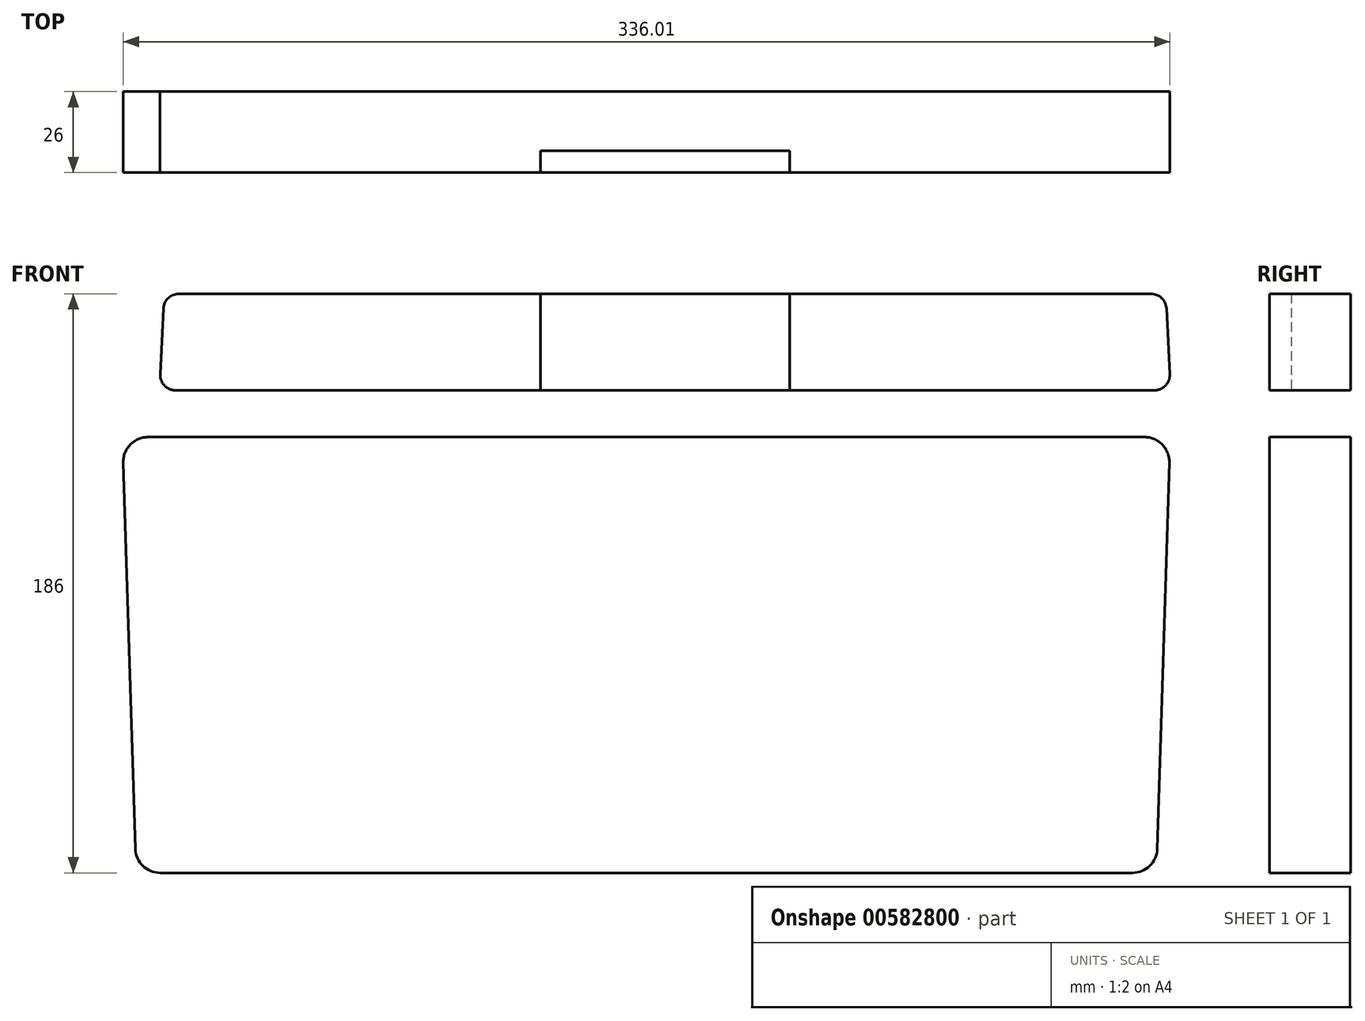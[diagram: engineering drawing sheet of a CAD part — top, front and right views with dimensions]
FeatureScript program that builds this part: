
annotation { "Feature Type Name" : "Feature", "Feature Type Description" : "" }
export const myFeature = defineFeature(function(context is Context, id is Id, definition is map)
    precondition{}
    {
        {
            var Q0;
            Q0=qCreatedBy(makeId("Front.planeOp"),FACE);
            var sketch = newSketch(context, id + "F0", { "sketchPlane" : qUnion([Q0])});
            skLineSegment(sketch, "E0.bottom", {"start": v(172.5, -161) * mm, "end": v(-172.5, -161) * mm});
            skLineSegment(sketch, "E0.top", {"start": v(177.5, -1) * mm, "end": v(-177.5, -1) * mm});
            skLineSegment(sketch, "E1.bottom", {"start": v(177.5, 1) * mm, "end": v(-177.5, 1) * mm});
            skLineSegment(sketch, "E1.top", {"start": v(175, 51) * mm, "end": v(-175, 51) * mm});
            skLineSegment(sketch, "E2", {"start": v(-177.5, -1) * mm, "end": v(-172.5, -161) * mm});
            skLineSegment(sketch, "E3", {"start": v(177.5, -1) * mm, "end": v(172.5, -161) * mm});
            skLineSegment(sketch, "E4", {"start": v(-177.5, 1) * mm, "end": v(-175, 51) * mm});
            skLineSegment(sketch, "E5", {"start": v(177.5, 1) * mm, "end": v(175, 51) * mm});
            skLineSegment(sketch, "E6.bottom", {"start": v(105.5, -101) * mm, "end": v(147.5, -101) * mm});
            skLineSegment(sketch, "E6.top", {"start": v(105.5, -161) * mm, "end": v(147.5, -161) * mm});
            skLineSegment(sketch, "E6.left", {"start": v(105.5, -101) * mm, "end": v(105.5, -161) * mm});
            skLineSegment(sketch, "E6.right", {"start": v(147.5, -101) * mm, "end": v(147.5, -161) * mm});
            skLineSegment(sketch, "E7.MirrorCS", {"start": v(-105.5, -101) * mm, "end": v(-105.5, -161) * mm});
            skLineSegment(sketch, "E8.MirrorCS", {"start": v(-105.5, -101) * mm, "end": v(-147.5, -101) * mm});
            skLineSegment(sketch, "E9.MirrorCS", {"start": v(-147.5, -101) * mm, "end": v(-147.5, -161) * mm});
            skSolve(sketch);
        }
        {
            var Q0;
            Q0=qCreatedBy(makeId("Front.planeOp"),FACE);
            var sketch = newSketch(context, id + "F1", { "sketchPlane" : qUnion([Q0])});
            skLineSegment(sketch, "E10", {"start": v(-159.68, -91) * mm, "end": v(-100.5, -91) * mm, "construction": true});
            skLineSegment(sketch, "E11", {"start": v(-100.5, -91) * mm, "end": v(-100.5, -151) * mm, "construction": true});
            skLineSegment(sketch, "E12", {"start": v(-100.5, -151) * mm, "end": v(100.5, -151) * mm});
            skLineSegment(sketch, "E13", {"start": v(100.5, -151) * mm, "end": v(100.5, -91) * mm, "construction": true});
            skLineSegment(sketch, "E14", {"start": v(100.5, -91) * mm, "end": v(152.5, -91) * mm, "construction": true});
            skLineSegment(sketch, "E15", {"start": v(152.5, -91) * mm, "end": v(152.5, -151) * mm, "construction": true});
            skLineSegment(sketch, "E16", {"start": v(152.5, -151) * mm, "end": v(169.81, -151) * mm});
            skLineSegment(sketch, "E17", {"start": v(169.81, -151) * mm, "end": v(174.19, -11) * mm});
            skLineSegment(sketch, "E18", {"start": v(174.19, -11) * mm, "end": v(-162.18, -11) * mm});
            skLineSegment(sketch, "E19", {"start": v(-162.18, -11) * mm, "end": v(-159.68, -91) * mm});
            skLineSegment(sketch, "E20", {"start": v(-159.68, -91) * mm, "end": v(-157.8, -151) * mm});
            skLineSegment(sketch, "E21", {"start": v(-157.8, -151) * mm, "end": v(-100.5, -151) * mm});
            skLineSegment(sketch, "E22", {"start": v(100.5, -151) * mm, "end": v(152.5, -151) * mm});
            skSolve(sketch);
        }
        {
            var Q0;
            Q0=qSketchRegion(id+"F1",true);
            extrude(context, id + "F2", {"entities" : qUnion([Q0]), "depth" : 26 * mm, "offsetDistance" : 25 * mm});
        }
        {
            var Q0;
            Q0=qCreatedBy(makeId("Front.planeOp"),FACE);
            var sketch = newSketch(context, id + "F3", { "sketchPlane" : qUnion([Q0])});
            skLineSegment(sketch, "E23.0", {"start": v(162.33, 4) * mm, "end": v(160.78, 35) * mm});
            skLineSegment(sketch, "E23.2", {"start": v(-162.33, 4) * mm, "end": v(-160.78, 35) * mm});
            skLineSegment(sketch, "E24", {"start": v(-160.78, 35) * mm, "end": v(160.78, 35) * mm});
            skLineSegment(sketch, "E25", {"start": v(-162.33, 4) * mm, "end": v(162.33, 4) * mm});
            skSolve(sketch);
        }
        {
            var Q0;
            Q0=qSketchRegion(id+"F3",true);
            var Q1;
            Q1=sQuery(id+"F3.wireOp",EDGE,"E24");
            var Q2;
            Q2=sQuery(id+"F3.wireOp",EDGE,"E23.2");
            var Q3;
            Q3=sQuery(id+"F3.wireOp",EDGE,"E25");
            var Q4;
            Q4=sQuery(id+"F3.wireOp",EDGE,"E23.0");
            extrude(context, id + "F4", {"entities" : qUnion([Q0]), "surfaceEntities" : qUnion([Q1, Q2, Q3, Q4]), "depth" : 26 * mm, "offsetDistance" : 25 * mm});
        }
        {
            var Q0;
            Q0=makeQuery(id+"F4.opExtrude","SWEPT_EDGE",EDGE,{"disambiguationData":[OSD([sQuery(id+"F3.wireOp",EDGE,"E23.2"),sQuery(id+"F3.wireOp",EDGE,"E24")])]});
            var Q1;
            Q1=makeQuery(id+"F4.opExtrude","SWEPT_EDGE",EDGE,{"disambiguationData":[OSD([sQuery(id+"F3.wireOp",EDGE,"E23.2"),sQuery(id+"F3.wireOp",EDGE,"E25")])]});
            var Q2;
            Q2=makeQuery(id+"F4.opExtrude","SWEPT_EDGE",EDGE,{"disambiguationData":[OSD([sQuery(id+"F3.wireOp",EDGE,"E23.0"),sQuery(id+"F3.wireOp",EDGE,"E24")])]});
            var Q3;
            Q3=makeQuery(id+"F4.opExtrude","SWEPT_EDGE",EDGE,{"disambiguationData":[OSD([sQuery(id+"F3.wireOp",EDGE,"E23.0"),sQuery(id+"F3.wireOp",EDGE,"E25")])]});
            fillet(context, id + "F5", {"entities" : qUnion([Q0, Q1, Q2, Q3]), "radius" : 5 * mm, "tangentPropagation" : true, "allowEdgeOverflow" : false});
        }
        {
            var Q0;
            Q0=makeQuery(id+"F4.opExtrude","CAP_FACE",FACE,{"disambiguationData":[OSD([sQuery(id+"F3.wireOp",EDGE,"E23.0"),sQuery(id+"F3.wireOp",EDGE,"E23.2"),sQuery(id+"F3.wireOp",EDGE,"E24"),sQuery(id+"F3.wireOp",EDGE,"E25")])],"isStart":false});
            var sketch = newSketch(context, id + "F6", { "sketchPlane" : qUnion([Q0])});
            skLineSegment(sketch, "E26", {"start": v(0, 4) * mm, "end": v(0, 35) * mm, "construction": true});
            skLineSegment(sketch, "E27", {"start": v(40, 35) * mm, "end": v(40, -1) * mm});
            skLineSegment(sketch, "E28.MirrorCS", {"start": v(-40, 35) * mm, "end": v(-40, -1) * mm});
            skLineSegment(sketch, "E29", {"start": v(-40, 35) * mm, "end": v(40, 35) * mm});
            skLineSegment(sketch, "E30", {"start": v(-40, -1) * mm, "end": v(40, -1) * mm});
            skPoint(sketch, "E31.orphan", {"position": v(-40, 4) * mm});
            skPoint(sketch, "E32.orphan", {"position": v(40, 4) * mm});
            skPoint(sketch, "E33.orphan", {"position": v(40, 35) * mm});
            skPoint(sketch, "E34.orphan", {"position": v(0, 35) * mm});
            skSolve(sketch);
        }
        {
            var Q0;
            Q0=qSketchRegion(id+"F6",true);
            extrude(context, id + "F7", {"entities" : qUnion([Q0]), "operationType" : NewBodyOperationType.REMOVE, "oppositeDirection" : true, "depth" : 7 * mm, "offsetDistance" : 25 * mm});
        }
        {
            var Q0;
            Q0=makeQuery(id+"F2.opExtrude","SWEPT_EDGE",EDGE,{"disambiguationData":[OSD([sQuery(id+"F1.wireOp",EDGE,"E15"),sQuery(id+"F1.wireOp",EDGE,"E16")])]});
            var Q1;
            Q1=makeQuery(id+"F2.opExtrude","SWEPT_EDGE",EDGE,{"disambiguationData":[OSD([sQuery(id+"F1.wireOp",EDGE,"E12"),sQuery(id+"F1.wireOp",EDGE,"E13")])]});
            var Q2;
            Q2=makeQuery(id+"F2.opExtrude","SWEPT_EDGE",EDGE,{"disambiguationData":[OSD([sQuery(id+"F1.wireOp",EDGE,"E16"),sQuery(id+"F1.wireOp",EDGE,"E17")])]});
            var Q3;
            Q3=makeQuery(id+"F2.opExtrude","SWEPT_EDGE",EDGE,{"disambiguationData":[OSD([sQuery(id+"F1.wireOp",EDGE,"E13"),sQuery(id+"F1.wireOp",EDGE,"E14")])]});
            var Q4;
            Q4=makeQuery(id+"F2.opExtrude","SWEPT_EDGE",EDGE,{"disambiguationData":[OSD([sQuery(id+"F1.wireOp",EDGE,"E14"),sQuery(id+"F1.wireOp",EDGE,"E15")])]});
            var Q5;
            Q5=makeQuery(id+"F2.opExtrude","SWEPT_EDGE",EDGE,{"disambiguationData":[OSD([sQuery(id+"F1.wireOp",EDGE,"E11"),sQuery(id+"F1.wireOp",EDGE,"E12")])]});
            var Q6;
            Q6=makeQuery(id+"F2.opExtrude","SWEPT_EDGE",EDGE,{"disambiguationData":[OSD([sQuery(id+"F1.wireOp",EDGE,"E10"),sQuery(id+"F1.wireOp",EDGE,"E11")])]});
            var Q7;
            Q7=makeQuery(id+"F2.opExtrude","SWEPT_EDGE",EDGE,{"disambiguationData":[OSD([sQuery(id+"F1.wireOp",EDGE,"E10"),sQuery(id+"F1.wireOp",EDGE,"E19")])]});
            var Q8;
            Q8=makeQuery(id+"F2.opExtrude","SWEPT_EDGE",EDGE,{"disambiguationData":[OSD([sQuery(id+"F1.wireOp",EDGE,"E18"),sQuery(id+"F1.wireOp",EDGE,"E19")])]});
            var Q9;
            Q9=makeQuery(id+"F2.opExtrude","SWEPT_EDGE",EDGE,{"disambiguationData":[OSD([sQuery(id+"F1.wireOp",EDGE,"E17"),sQuery(id+"F1.wireOp",EDGE,"E18")])]});
            var Q10;
            Q10=makeQuery(id+"F2.opExtrude","SWEPT_EDGE",EDGE,{"disambiguationData":[OSD([sQuery(id+"F1.wireOp",EDGE,"E20"),sQuery(id+"F1.wireOp",EDGE,"E21")])]});
            fillet(context, id + "F8", {"entities" : qUnion([Q0, Q1, Q2, Q3, Q4, Q5, Q6, Q7, Q8, Q9, Q10]), "radius" : 8 * mm, "tangentPropagation" : true, "allowEdgeOverflow" : false});
        }
        {
            var Q0;
            Q0=qCreatedBy(makeId("Right.planeOp"),FACE);
            cPlane(context, id + "F9", {"entities" : qUnion([Q0]), "cplaneType" : CPlaneType.OFFSET, "offset" : 165 * mm, "oppositeDirection" : true, "width" : 150 * mm, "height" : 150 * mm});
        }
        {
            var Q0;
            Q0=makeQuery(id+"F4.opExtrude","SWEPT_BODY",BODY,{"disambiguationData":[OSD([sQuery(id+"F3.wireOp",EDGE,"E23.0"),sQuery(id+"F3.wireOp",EDGE,"E23.2"),sQuery(id+"F3.wireOp",EDGE,"E24"),sQuery(id+"F3.wireOp",EDGE,"E25")])]});
            var Q1;
            Q1=makeQuery(id+"F2.opExtrude","SWEPT_BODY",BODY,{"disambiguationData":[OSD([sQuery(id+"F1.wireOp",EDGE,"E10"),sQuery(id+"F1.wireOp",EDGE,"E11"),sQuery(id+"F1.wireOp",EDGE,"E12"),sQuery(id+"F1.wireOp",EDGE,"E13"),sQuery(id+"F1.wireOp",EDGE,"E14"),sQuery(id+"F1.wireOp",EDGE,"E15"),sQuery(id+"F1.wireOp",EDGE,"E16"),sQuery(id+"F1.wireOp",EDGE,"E17"),sQuery(id+"F1.wireOp",EDGE,"E18"),sQuery(id+"F1.wireOp",EDGE,"E19")])]});
            var Q2;
            Q2=qCreatedBy(id+"F9.planeOp",FACE);
            mirror(context, id + "F10", {"entities" : qUnion([Q0, Q1]), "mirrorPlane" : qUnion([Q2])});
        }
        {
            var Q0;
            Q0=qCreatedBy(makeId("Front.planeOp"),FACE);
            var sketch = newSketch(context, id + "F11", { "sketchPlane" : qUnion([Q0])});
            skLineSegment(sketch, "E35.bottom", {"start": v(177.5, -209.44) * mm, "end": v(-165, -209.44) * mm});
            skLineSegment(sketch, "E35.top", {"start": v(177.5, 209.44) * mm, "end": v(-165, 209.44) * mm});
            skLineSegment(sketch, "E35.left", {"start": v(177.5, -209.44) * mm, "end": v(177.5, 209.44) * mm});
            skLineSegment(sketch, "E35.right", {"start": v(-165, -209.44) * mm, "end": v(-165, 209.44) * mm});
            skPoint(sketch, "E35.middle", {"position": v(6.25, 0) * mm});
            skSolve(sketch);
        }
        {
            var Q0;
            Q0 = qSketchRegion(id + "F11", true);
            extrude(context, id + "F12", {"entities" : qUnion([Q0]), "operationType" : NewBodyOperationType.REMOVE, "endBound" : BoundingType.THROUGH_ALL, "depth" : 25 * mm, "offsetDistance" : 25 * mm});
        }
    });
